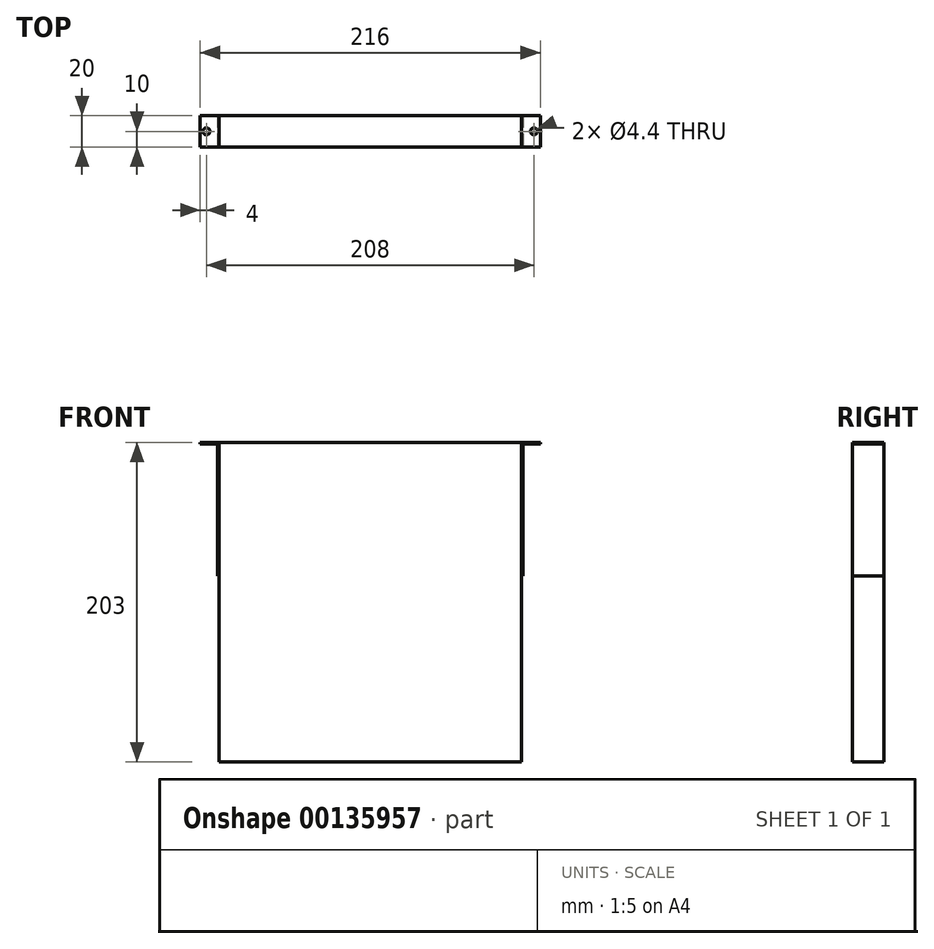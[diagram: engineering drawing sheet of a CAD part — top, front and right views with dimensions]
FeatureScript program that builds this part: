
annotation { "Feature Type Name" : "Feature", "Feature Type Description" : "" }
export const myFeature = defineFeature(function(context is Context, id is Id, definition is map)
    precondition{}
    {
        {
            var Q0;
            Q0=qCreatedBy(makeId("Front.planeOp"),FACE);
            var sketch = newSketch(context, id + "F0", { "sketchPlane" : qUnion([Q0])});
            skLineSegment(sketch, "E0.bottom", {"start": v(96, -101.5) * mm, "end": v(-96, -101.5) * mm});
            skLineSegment(sketch, "E0.top", {"start": v(96, 101.5) * mm, "end": v(-96, 101.5) * mm});
            skLineSegment(sketch, "E0.left", {"start": v(96, -101.5) * mm, "end": v(96, 101.5) * mm});
            skLineSegment(sketch, "E0.right", {"start": v(-96, -101.5) * mm, "end": v(-96, 101.5) * mm});
            skPoint(sketch, "E0.middle", {"position": v(0, 0) * mm});
            skSolve(sketch);
        }
        {
            var Q0;
            Q0=qSketchRegion(id+"F0",true);
            extrude(context, id + "F1", {"entities" : qUnion([Q0]), "depth" : 20 * mm});
        }
        {
            var Q0;
            Q0=makeQuery(id+"F1.opExtrude","CAP_FACE",FACE,{"disambiguationData":[OSD([sQuery(id+"F0.wireOp",EDGE,"E0.bottom"),sQuery(id+"F0.wireOp",EDGE,"E0.top"),sQuery(id+"F0.wireOp",EDGE,"E0.left"),sQuery(id+"F0.wireOp",EDGE,"E0.right")])],"isStart":false});
            var sketch = newSketch(context, id + "F2", { "sketchPlane" : qUnion([Q0])});
            skLineSegment(sketch, "E1.bottom", {"start": v(-96, 101.5) * mm, "end": v(-97, 101.5) * mm});
            skLineSegment(sketch, "E1.top", {"start": v(-96, 16.5) * mm, "end": v(-97, 16.5) * mm});
            skLineSegment(sketch, "E1.left", {"start": v(-96, 101.5) * mm, "end": v(-96, 16.5) * mm});
            skLineSegment(sketch, "E1.right", {"start": v(-97, 100.5) * mm, "end": v(-97, 16.5) * mm});
            skLineSegment(sketch, "E2.bottom", {"start": v(-97, 101.5) * mm, "end": v(-108, 101.5) * mm});
            skLineSegment(sketch, "E2.top", {"start": v(-97, 100.5) * mm, "end": v(-108, 100.5) * mm});
            skLineSegment(sketch, "E2.right", {"start": v(-108, 101.5) * mm, "end": v(-108, 100.5) * mm});
            skLineSegment(sketch, "E3.MirrorCS", {"start": v(108, 101.5) * mm, "end": v(108, 100.5) * mm});
            skLineSegment(sketch, "E4.MirrorCS", {"start": v(97, 101.5) * mm, "end": v(108, 101.5) * mm});
            skLineSegment(sketch, "E5.MirrorCS", {"start": v(97, 100.5) * mm, "end": v(108, 100.5) * mm});
            skLineSegment(sketch, "E6.MirrorCS", {"start": v(96, 101.5) * mm, "end": v(97, 101.5) * mm});
            skLineSegment(sketch, "E7.MirrorCS", {"start": v(96, 101.5) * mm, "end": v(96, 16.5) * mm});
            skLineSegment(sketch, "E8.MirrorCS", {"start": v(97, 100.5) * mm, "end": v(97, 16.5) * mm});
            skLineSegment(sketch, "E9.MirrorCS", {"start": v(96, 16.5) * mm, "end": v(97, 16.5) * mm});
            skSolve(sketch);
        }
        {
            var Q0;
            Q0=qSketchRegion(id+"F2",true);
            extrude(context, id + "F3", {"entities" : qUnion([Q0]), "oppositeDirection" : true, "depth" : 20 * mm});
        }
        {
            var Q0;
            Q0=makeQuery(id+"F3.opExtrude","SWEPT_FACE",FACE,{"disambiguationData":[OSD([sQuery(id+"F2.wireOp",EDGE,"E1.bottom"),sQuery(id+"F2.wireOp",EDGE,"E2.bottom")])]});
            var sketch = newSketch(context, id + "F4", { "sketchPlane" : qUnion([Q0])});
            skCircle(sketch, "E10", {"center": v(-104, -10) * mm, "radius": 2 * mm});
            skCircle(sketch, "E11.MirrorC", {"center": v(104, -10) * mm, "radius": 2 * mm});
            skSolve(sketch);
        }
        {
            var Q0;
            Q0=sQuery(id+"F4.wireOp",VERTEX,"E10.center");
            var Q1;
            Q1=sQuery(id+"F4.wireOp",VERTEX,"E11.MirrorC.center");
            var Q2;
            Q2=makeQuery(id+"F3.opExtrude","SWEPT_BODY",BODY,{"disambiguationData":[OSD([sQuery(id+"F2.wireOp",EDGE,"E1.bottom"),sQuery(id+"F2.wireOp",EDGE,"E1.top"),sQuery(id+"F2.wireOp",EDGE,"E1.left"),sQuery(id+"F2.wireOp",EDGE,"E1.right"),sQuery(id+"F2.wireOp",EDGE,"E2.bottom"),sQuery(id+"F2.wireOp",EDGE,"E2.top"),sQuery(id+"F2.wireOp",EDGE,"E2.right")])]});
            var Q3;
            Q3=makeQuery(id+"F3.opExtrude","SWEPT_BODY",BODY,{"disambiguationData":[OSD([sQuery(id+"F2.wireOp",EDGE,"E3.MirrorCS"),sQuery(id+"F2.wireOp",EDGE,"E4.MirrorCS"),sQuery(id+"F2.wireOp",EDGE,"E5.MirrorCS"),sQuery(id+"F2.wireOp",EDGE,"E6.MirrorCS"),sQuery(id+"F2.wireOp",EDGE,"E7.MirrorCS"),sQuery(id+"F2.wireOp",EDGE,"E8.MirrorCS"),sQuery(id+"F2.wireOp",EDGE,"E9.MirrorCS")])]});
            hole(context, id + "F5", {"style" : HoleStyle.SIMPLE, "endStyle" : HoleEndStyle.BLIND, "standardTappedOrClearance" : lookupTablePath({ "standard" : "ISO", "fit" : "Normal", "size" : "M4", "type" : "Clearance" }), "standardBlindInLast" : lookupTablePath({ "fit" : "Standard", "standard" : "ISO", "size" : "M4", "type" : "Clearance" }), "holeDiameter" : 4.4 * mm, "holeDepth" : 12 * mm, "startFromSketch" : true, "locations" : qUnion([Q0, Q1]), "scope" : qUnion([Q2, Q3])});
        }
    });
